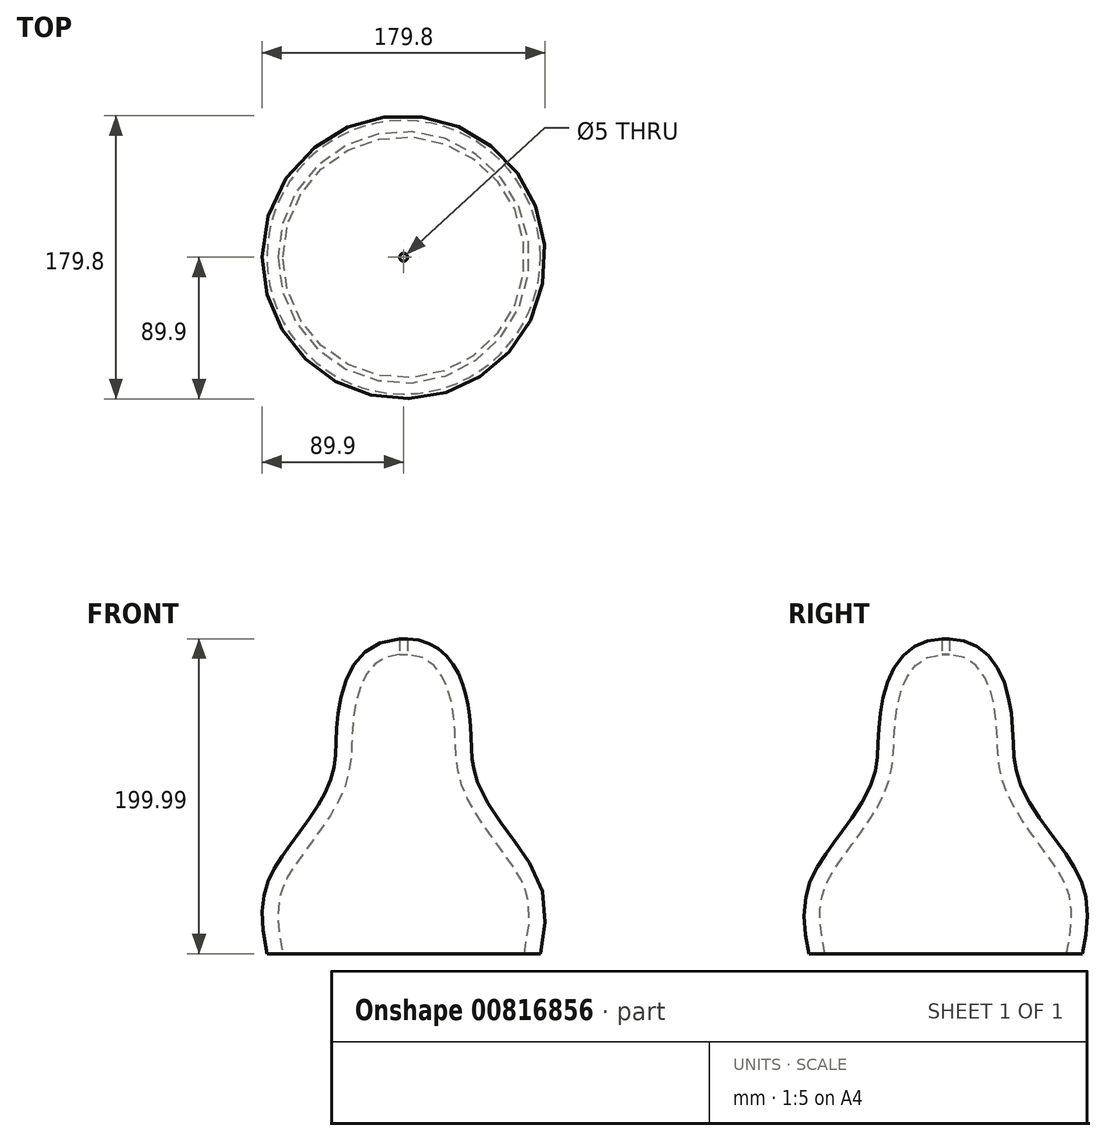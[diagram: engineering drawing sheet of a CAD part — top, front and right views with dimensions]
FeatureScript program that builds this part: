
annotation { "Feature Type Name" : "Feature", "Feature Type Description" : "" }
export const myFeature = defineFeature(function(context is Context, id is Id, definition is map)
    precondition{}
    {
        {
            var Q0;
            Q0=qCreatedBy(makeId("Front.planeOp"),FACE);
            var sketch = newSketch(context, id + "F0", { "sketchPlane" : qUnion([Q0])});
            skLineSegment(sketch, "E0", {"start": v(0, 0) * mm, "end": v(0, 232.53) * mm, "construction": true});
            skFitSpline(sketch, "E1", {"points": [v(0, 200) * mm, v(41.52, 153.42) * mm, v(46.5, 110.05) * mm, v(76.36, 63.13) * mm, v(86.88, 0) * mm], "startDerivative": vector(340.49, 7) * mm, "endDerivative": vector(-81.53, -373.84) * mm});
            skLineSegment(sketch, "E2", {"start": v(86.88, 0) * mm, "end": v(0, 0) * mm});
            skLineSegment(sketch, "E3", {"start": v(0, 200) * mm, "end": v(0, 0) * mm});
            skSolve(sketch);
        }
        {
            var Q0;
            Q0=makeQuery(id+"F0.imprint","IMPRINT",FACE,{"disambiguationData":[TD([[makeQuery(id+"F0.imprint","IMPRINT",EDGE,{"derivedFrom":sQuery(id+"F0.wireOp",EDGE,"E1")}),-1.0]])]});
            var Q1;
            Q1=sQuery(id+"F0.wireOp",EDGE,"E0");
            revolve(context, id + "F1", {"surfaceOperationType" : NewSurfaceOperationType.NEW, "entities" : qUnion([Q0]), "axis" : qUnion([Q1]), "revolveType" : RevolveType.FULL});
        }
        {
            var Q0;
            Q0=makeQuery(id+"F1.opRevolve","SWEPT_FACE",FACE,{"disambiguationData":[OSD([sQuery(id+"F0.wireOp",EDGE,"E2")])]});
            shell(context, id + "F2", {"entities" : qUnion([Q0]), "thickness" : 10 * mm});
        }
        {
            var Q0;
            Q0=qCreatedBy(makeId("Top.planeOp"),FACE);
            var sketch = newSketch(context, id + "F3", { "sketchPlane" : qUnion([Q0])});
            skCircle(sketch, "E4", {"center": v(0, 0) * mm, "radius": 5 * mm});
            skSolve(sketch);
        }
        {
            var Q0;
            Q0=sQuery(id+"F3.wireOp",VERTEX,"E4.center");
            var Q1;
            Q1=makeQuery(id+"F1.opRevolve","SWEPT_BODY",BODY,{"disambiguationData":[OSD([sQuery(id+"F0.wireOp",EDGE,"E1"),sQuery(id+"F0.wireOp",EDGE,"E2"),sQuery(id+"F0.wireOp",EDGE,"E3")])]});
            hole(context, id + "F4", {"style" : HoleStyle.SIMPLE, "endStyle" : HoleEndStyle.THROUGH, "oppositeDirection" : true, "holeDiameter" : 5 * mm, "majorDiameter" : 5 * mm, "isTappedThrough" : true, "tappedDepth" : 12 * mm, "tapClearance" : 3, "locations" : qUnion([Q0]), "scope" : qUnion([Q1])});
        }
    });
